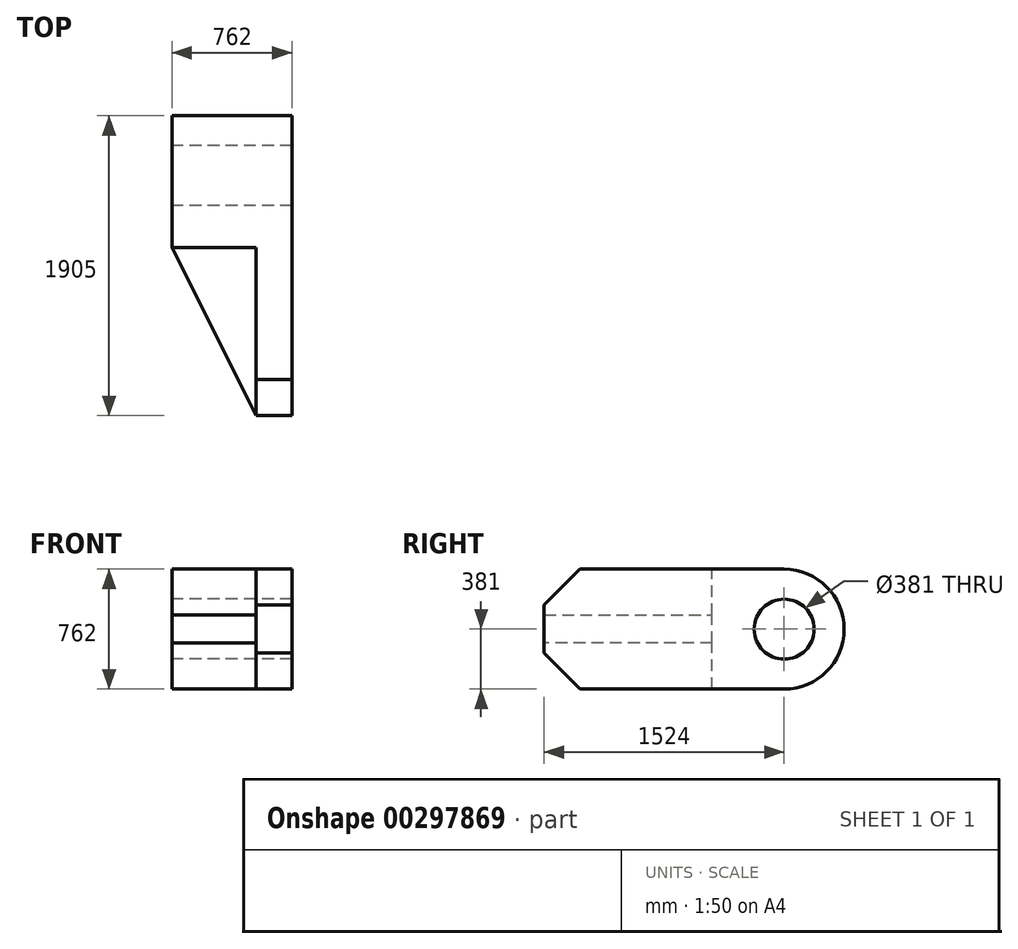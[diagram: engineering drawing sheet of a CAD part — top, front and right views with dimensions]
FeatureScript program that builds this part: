
annotation { "Feature Type Name" : "Feature", "Feature Type Description" : "" }
export const myFeature = defineFeature(function(context is Context, id is Id, definition is map)
    precondition{}
    {
        {
            var Q0;
            Q0=qCreatedBy(makeId("Right.planeOp"),FACE);
            var sketch = newSketch(context, id + "F0", { "sketchPlane" : qUnion([Q0])});
            skLineSegment(sketch, "E0.bottom", {"start": v(-533.4, 381) * mm, "end": v(762, 381) * mm});
            skLineSegment(sketch, "E0.top", {"start": v(-533.4, -381) * mm, "end": v(762, -381) * mm});
            skLineSegment(sketch, "E0.left", {"start": v(-762, 152.4) * mm, "end": v(-762, -152.4) * mm});
            skPoint(sketch, "E0.middle", {"position": v(0, 0) * mm});
            skArc(sketch, "E1", {"start": v(762, -381) * mm, "mid": v(1143, 0) * mm, "end": v(762, 381) * mm});
            skLineSegment(sketch, "E2", {"start": v(-533.4, 381) * mm, "end": v(-762, 152.4) * mm});
            skLineSegment(sketch, "E3", {"start": v(-762, -152.4) * mm, "end": v(-533.4, -381) * mm});
            skPoint(sketch, "E4.orphan", {"position": v(-762, 381) * mm});
            skPoint(sketch, "E5.orphan", {"position": v(-762, -381) * mm});
            skSolve(sketch);
        }
        {
            var Q0;
            Q0 = qSketchRegion(id + "F0", true);
            extrude(context, id + "F1", {"entities" : qUnion([Q0]), "oppositeDirection" : true, "depth" : 228.6 * mm});
        }
        {
            var Q0;
            Q0=makeQuery(id+"F1.opExtrude","CAP_FACE",FACE,{"disambiguationData":[OSD([sQuery(id+"F0.wireOp",EDGE,"E0.bottom"),sQuery(id+"F0.wireOp",EDGE,"E0.top"),sQuery(id+"F0.wireOp",EDGE,"E0.left"),sQuery(id+"F0.wireOp",EDGE,"E1"),sQuery(id+"F0.wireOp",EDGE,"E2"),sQuery(id+"F0.wireOp",EDGE,"E3")])],"isStart":false});
            var sketch = newSketch(context, id + "F2", { "sketchPlane" : qUnion([Q0])});
            skLineSegment(sketch, "E6", {"start": v(-762, -381) * mm, "end": v(-304.8, -381) * mm});
            skLineSegment(sketch, "E7", {"start": v(-304.8, -381) * mm, "end": v(-304.8, -88.9) * mm});
            skLineSegment(sketch, "E8", {"start": v(-304.8, -88.9) * mm, "end": v(762, -88.9) * mm});
            skLineSegment(sketch, "E9", {"start": v(762, -88.9) * mm, "end": v(762, 88.9) * mm});
            skLineSegment(sketch, "E10", {"start": v(762, 88.9) * mm, "end": v(-304.8, 88.9) * mm});
            skLineSegment(sketch, "E11", {"start": v(-304.8, 88.9) * mm, "end": v(-304.8, 381) * mm});
            skLineSegment(sketch, "E12", {"start": v(-304.8, 381) * mm, "end": v(-762, 381) * mm});
            skArc(sketch, "E13", {"start": v(-762, 381) * mm, "mid": v(-1143, 0) * mm, "end": v(-762, -381) * mm});
            skSolve(sketch);
        }
        {
            var Q0;
            Q0 = qSketchRegion(id + "F2", true);
            extrude(context, id + "F3", {"entities" : qUnion([Q0]), "operationType" : NewBodyOperationType.ADD, "depth" : 533.4 * mm});
        }
        {
            var Q0;
            Q0=makeQuery(id+"F3.opExtrude","CAP_EDGE",EDGE,{"disambiguationData":[OSD([sQuery(id+"F2.wireOp",EDGE,"E9")])],"isStart":false});
            chamfer(context, id + "F4", {"entities" : qUnion([Q0]), "chamferType" : ChamferType.OFFSET_ANGLE, "width" : 533.4 * mm, "oppositeDirection" : false, "angle" : 63.43 * degree, "tangentPropagation" : true});
        }
        {
            var Q0;
            Q0=makeQuery(id+"F3.opExtrude","CAP_FACE",FACE,{"disambiguationData":[OSD([sQuery(id+"F2.wireOp",EDGE,"E6"),sQuery(id+"F2.wireOp",EDGE,"E7"),sQuery(id+"F2.wireOp",EDGE,"E8"),sQuery(id+"F2.wireOp",EDGE,"E9"),sQuery(id+"F2.wireOp",EDGE,"E10"),sQuery(id+"F2.wireOp",EDGE,"E11"),sQuery(id+"F2.wireOp",EDGE,"E12"),sQuery(id+"F2.wireOp",EDGE,"E13")])],"isStart":false});
            var sketch = newSketch(context, id + "F5", { "sketchPlane" : qUnion([Q0])});
            skCircle(sketch, "E14", {"center": v(-762, 0) * mm, "radius": 190.5 * mm});
            skSolve(sketch);
        }
        {
            var Q0;
            Q0 = qSketchRegion(id + "F5", true);
            extrude(context, id + "F6", {"entities" : qUnion([Q0]), "operationType" : NewBodyOperationType.REMOVE, "oppositeDirection" : true, "depth" : 762 * mm});
        }
    });
